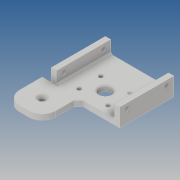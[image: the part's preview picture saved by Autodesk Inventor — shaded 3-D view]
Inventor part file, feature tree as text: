
AUTODESK INVENTOR PART (.ipt)
format: ipt  version: 2019 (Build 230136000, 136)  size: 171,520 bytes
history: native  units: mm
features: other x3, sketch x3, hole x2, extrude x2, chamfer x2, fillet x1
ambient origin geometry x8: Origin, YZ Plane, XZ Plane, XY Plane, X Axis, Y Axis, Z Axis, Center Point
bodies: Solide1 (feature_tree)
feature tree (13):
  other  "base_cloison.ipt"
  sketch  "Esquisse1"
  hole  "Perçage1"  [1 undecoded]
  extrude  "Extrusion1"  Depth=18.0mm
  chamfer  "Chanfrein1"  Distance=40.0mm
  extrude  "Extrusion2"  Depth=47.0mm
  hole  "Perçage2"  [1 undecoded]
  chamfer  "Chanfrein3"  Distance=4.0mm
  fillet  "Congé1"  Radius=4.0mm
  other  "Solide1::base_cloison.ipt"
  other  "FonctionRepérage1"
  sketch  "Esquisse2"
  sketch  "Esquisse4"
note: 2 required parameter values undecoded (feature->parameter linkage not recoverable at this tier; creation-order binding heuristic only, values carry confidence <= 0.55)
